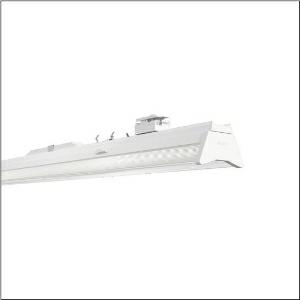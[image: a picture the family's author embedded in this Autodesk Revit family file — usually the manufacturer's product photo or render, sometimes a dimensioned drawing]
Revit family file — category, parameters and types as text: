
# Revit family: licross_r__11_performance_mo_51tm16cn49xg_d1b9
name_source: partatom
category: Lighting Fixtures
units: mm (PartAtom-declared; Revit-internal decimal feet)

## family parameters
Cut with Voids When Loaded = No
Host = Face
Light Source = No
Part Type = Normal
Room Calculation Point = No
Round Connector Dimension = Use Diameter
Shared = No

## types (1)
- --- (1 x LED, 9190 lm, 49.4 W, 4000K)
    Apparent Load = 49 VA
    CIE Flux Codes = 66 88 96 79 100
    Color Rendering = 80
    Color Temperature = 4000K
    Default Elevation = 1800 mm
    Description = Licross® 11 Performance MO, luminaire insert, of sheet steel, galvanised, coil coated, white, length: 1.500mm, width: 120mm, height: 123mm, LED rated luminous flux: 9.190lm, light colour: 840, control gear: ON/OFF Multilumen, CLOi, with plug, 3-pole, with phase selection, mains connection: 220..240V, AC, 50/60Hz, start of lifetime: 49W, end of service life: 55W, internal wiring halogen-free, primary light control with lens, of plastic, primary optical cover: cover, of PMMA, light emission: direct/indirect distribution, primary light characteristic: symmetric, protection rating (complete): IP40, insulation class (complete): insulation class I (protective earthing), certification: CE, ENEC, VDE, UKCA, protection symbol: D if used in an environment without relevant dust loads with corresponding accessories, impact resistance: IK06, permissible ambient temperature for indoor applications: -35..+40°C, corresponds to IFS (International Featured Standards) requirements for safety and quality in the food industry, reducing of maximum allowable ambient temperature of 5°C with ceiling mounting, LABS conformity tested according to VDMA 24364:2018-05, packaging unit: 1 piece
    Height = 114 mm
    Lamp = 1 x LED
    Lamp Light Flux = 9190 lm
    Lamp Power = 49.4 W
    Lamp count = 1
    Length = 1500 mm
    Luminous efficacy = 186 lm/W
    Manufacturer = Siteco
    ModVariant = No
    Model = 51TM16CN49XG
    Mounting Place = Ceiling
    Mounting Type = Pendant
    Number of Poles = 1
    OnlyDefault = Yes
    Power Factor = 1
    Product Name = Licross® 11 Performance MO
    Product group = luminaire insert | ceiling pendant
    ProductGroupID = 902
    Protection Class = Protection class I
    Protection Degree = IP 40
    RLX_Detail_Level = 1
    RLX_Emergency_Light_Flux = 0 lm
    RLX_Emergency_Type = 0
    RLX_Emergency_Type_DB = No
    RlxData = <blob elided: 31821 chars, md5=5c5966db>
    Socket = socket
    Standby Power = 0 W
    System Light Flux = 9190 lm
    System Power = 49 W
    Type Comments = factory setting: luminous flux: 100 % | (A | C | E) | 113 mA
    Type Image = l_1256138.jpg
    URL = http://relux.com
    VarID = @adj_107603
    Voltage = 0 V
    Weight = 0.00 kg
    Width = 120 mm

## geometry (parser evidence)
native form markers: Blend x4, Sweep x11
no freeform markers — native parametric forms only
